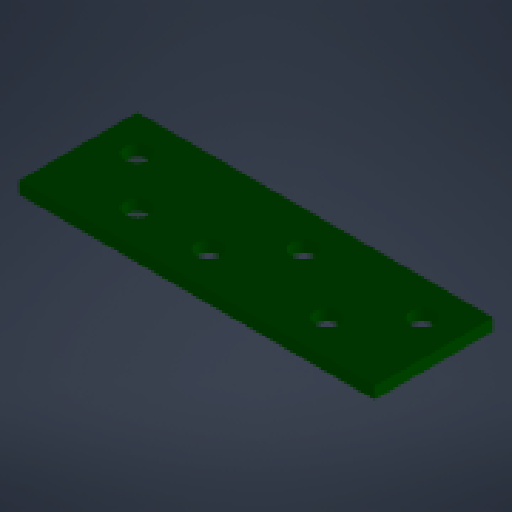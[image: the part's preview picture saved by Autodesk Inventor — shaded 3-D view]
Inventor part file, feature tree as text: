
AUTODESK INVENTOR PART (.ipt)
format: ipt  version: 2024 (Build 280153000, 153)  size: 139,264 bytes
history: native  units: mm
features: reference x9, other x6, extrude x1, sketch x1
ambient origin geometry x8: Origin, YZ Plane, XZ Plane, XY Plane, X Axis, Y Axis, Z Axis, Center Point
bodies: Body1 (feature_tree)
feature tree (17):
  other  "Твердое тело1"
  extrude  "Выдавливание1"  Depth=60.0mm
  sketch  "Эскиз1"
  reference  "Ссылка1"
  reference  "Ссылка2"
  reference  "Ссылка3"
  reference  "Ссылка4"
  reference  "Ссылка5"
  reference  "Ссылка6"
  reference  "Ссылка7"
  reference  "Ссылка8"
  reference  "Ссылка9"
  parser-record x1  (decoder bookkeeping rows leaked as tree rows — omitted from the tree; the rows remain in map.json)
  other  "base_assembly.iam"
  other  "square_box_section:1"
  other  "square_box_side_section:1"
  other  "square_box_side_section:2"
note: 1 file-system path scrubbed to <path> (originals preserved in map.json)
